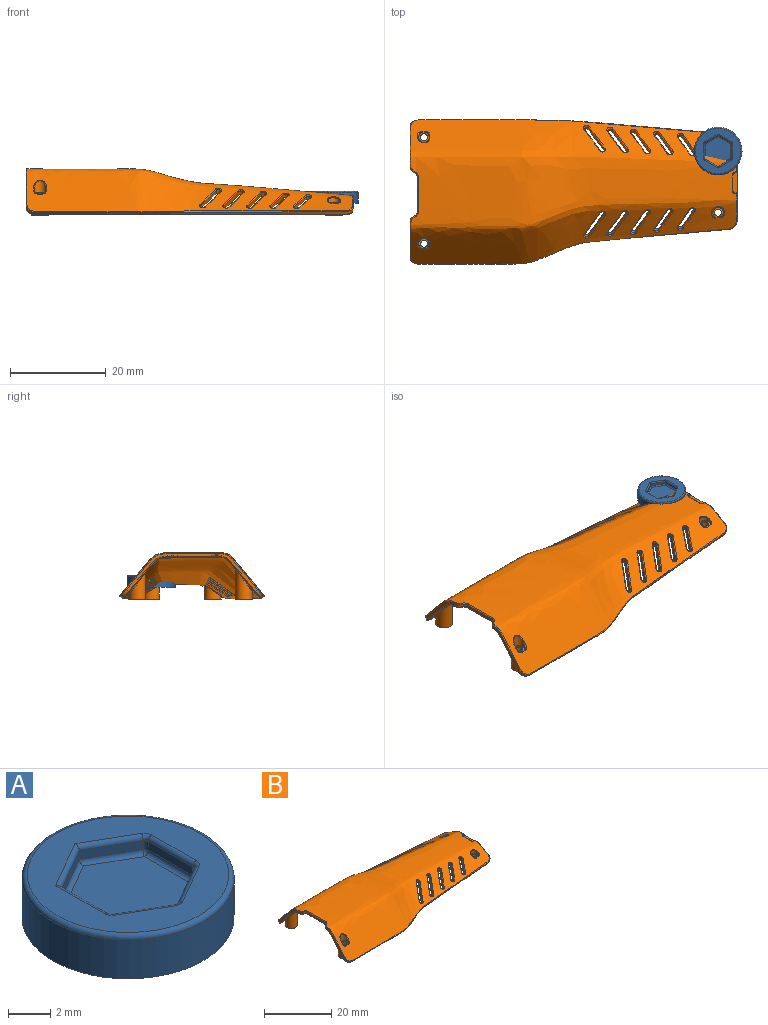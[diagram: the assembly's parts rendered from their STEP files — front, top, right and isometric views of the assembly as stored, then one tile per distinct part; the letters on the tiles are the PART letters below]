
ASSEMBLY  parts=2 mates=1
PART A: 35 faces, bbox 10.8x10.8x2.5 mm
  f0: plane 9.5x9.5mm, normal (0,0,1), area 38.4mm2, adj f16,f20,f21,f25,f26,f28,f29,f31
  f1: cylinder r=5mm len=10mm, axis (0,0,-1), area 70.7mm2, adj f2,f34
  f2: plane 10x10mm, normal (0,0,-1), area 78.5mm2, adj f1
  f3: plane 2.56x1.48mm, normal (0.5,0.87,0), area 1.5mm2, adj f11,f12,f19,f20
  f4: plane 2.56x1.48mm, normal (-0.5,0.87,0), area 1.5mm2, adj f12,f13,f21,f22
  f5: plane 2.96x0.5mm, normal (-1,0,0), area 1.5mm2, adj f22,f23,f29,f30
  f6: plane 2.69x1.55mm, normal (-0.5,-0.87,0), area 1.6mm2, adj f7,f24,f30,f33
  f7: plane 2.81x1.63mm, normal (0.5,-0.87,0), area 1.6mm2, adj f6,f8,f18,f31
  f8: plane 3.11x0.5mm, normal (1,0,0), area 1.6mm2, adj f7,f14,f19,f28
  f9: plane 5.92x5.13mm, normal (0,0,1), area 22.8mm2, adj f11,f13,f14,f18,f23,f24
  f10: sphere r=0.25mm, area 0.1mm2, adj f11,f12,f13
  f11: cylinder r=0.25mm len=2.69mm, axis (0.87,-0.5,0), area 1.2mm2, adj f3,f9,f10,f15
  f12: cylinder r=0.25mm len=0.5mm, axis (0,0,-1), area 0.1mm2, adj f3,f4,f10,f16
  f13: cylinder r=0.25mm len=2.69mm, axis (0.87,0.5,0), area 1.2mm2, adj f4,f9,f10,f17
  f14: cylinder r=0.25mm len=3.11mm, axis (0,-1,0), area 1.2mm2, adj f8,f9,f15,f18
  f15: sphere r=0.25mm, area 0.1mm2, adj f11,f14,f19
  f16: torus R=0.5mm, axis (0,0,1), area 0.1mm2, adj f0,f12,f20,f21
  f17: sphere r=0.25mm, area 0.1mm2, adj f13,f22,f23
  f18: cylinder r=0.25mm len=2.94mm, axis (-0.87,-0.5,0), area 1.2mm2, adj f7,f9,f14,f24
  f19: cylinder r=0.25mm len=0.5mm, axis (0,0,-1), area 0.1mm2, adj f3,f8,f15,f25
  f20: cylinder r=0.25mm len=2.69mm, axis (-0.87,0.5,0), area 1.2mm2, adj f0,f3,f16,f25
  f21: cylinder r=0.25mm len=2.69mm, axis (-0.87,-0.5,0), area 1.2mm2, adj f0,f4,f16,f26
  f22: cylinder r=0.25mm len=0.5mm, axis (0,0,-1), area 0.1mm2, adj f4,f5,f17,f26
  f23: cylinder r=0.25mm len=2.96mm, axis (0,1,0), area 1.2mm2, adj f5,f9,f17,f27
  f24: cylinder r=0.25mm len=2.81mm, axis (-0.87,0.5,0), area 1.2mm2, adj f6,f9,f18,f27
  f25: torus R=0.5mm, axis (0,0,1), area 0.1mm2, adj f0,f19,f20,f28
  f26: torus R=0.5mm, axis (0,0,1), area 0.1mm2, adj f0,f21,f22,f29
  f27: sphere r=0.25mm, area 0.1mm2, adj f23,f24,f30
  f28: cylinder r=0.25mm len=3.25mm, axis (0,1,0), area 1.2mm2, adj f0,f8,f25,f31
  f29: cylinder r=0.25mm len=2.96mm, axis (0,-1,0), area 1.2mm2, adj f0,f5,f26,f32
  f30: cylinder r=0.25mm len=0.5mm, axis (0,0,-1), area 0.1mm2, adj f5,f6,f27,f32
  f31: cylinder r=0.25mm len=3.19mm, axis (0.87,0.5,0), area 1.3mm2, adj f0,f7,f28,f33
  f32: torus R=0.5mm, axis (0,0,1), area 0.1mm2, adj f0,f29,f30,f33
  f33: cylinder r=0.25mm len=2.94mm, axis (0.87,-0.5,0), area 1.2mm2, adj f0,f6,f31,f32
  f34: torus R=4.75mm, axis (0,0,1), area 12.1mm2, adj f0,f1
PART B: 192 faces, bbox 76.3x36.1x14.9 mm
  f0: offset ~73.33x31.03mm, area 1976.2mm2, adj f1,f114,f115,f116,f117,f118,f119,f120
  f1: bspline ~2.79x2.08mm, area 1.4mm2, adj f0,f2,f114,f116
  f2: cylinder r=1.2mm len=2.39mm, axis (0,0,1), area 0mm2, adj f1,f3
  f3: torus R=1.1mm, axis (0,0,1), area 0.8mm2, adj f2,f4,f114,f116
  f4: plane 2.19x2.1mm, normal (0,0,1), area 2mm2, adj f3,f5,f115
  f5: cylinder r=0.72mm len=2.5mm, axis (0,0,-1), area 11.4mm2, adj f4,f6
  f6: plane 3.46x3.46mm, normal (0,0,-1), area 7.8mm2, adj f5,f7
  f7: cylinder r=1.73mm len=3.46mm, axis (0,0,-1), area 18.4mm2, adj f6,f8
  f8: bspline ~3.87x3.87mm, area 3.9mm2, adj f7,f9
  f9: bspline ~71.92x28.74mm, area 1873.9mm2, adj f8,f10,f11,f12,f13,f14,f15,f16
  f10: plane 4.4x3.43mm, normal (0.86,-0.42,-0.3), area 4.6mm2, adj f9,f11,f13,f168
  f11: cylinder r=0.5mm len=1.16mm, axis (0.06,-0.49,0.87), area 1.3mm2, adj f9,f10,f12,f169
  f12: plane 4.39x3.4mm, normal (-0.86,0.42,0.3), area 4.4mm2, adj f9,f11,f13,f170
  f13: cylinder r=0.5mm len=1.17mm, axis (0.06,-0.49,0.87), area 1.3mm2, adj f9,f10,f12,f171
  f14: plane 3.96x2.85mm, normal (0.86,-0.42,-0.3), area 3.9mm2, adj f9,f15,f17,f160
  f15: cylinder r=0.5mm len=1.13mm, axis (0.06,-0.49,0.87), area 1.3mm2, adj f9,f14,f16,f161
  f16: plane 4.51x3.37mm, normal (-0.86,0.42,0.3), area 3.8mm2, adj f9,f15,f17,f162
  f17: cylinder r=0.5mm len=1.14mm, axis (0.06,-0.49,0.87), area 1.3mm2, adj f9,f14,f16,f163
  f18: plane 4.91x3.9mm, normal (0.86,-0.42,-0.3), area 5.3mm2, adj f9,f19,f21,f152
  f19: cylinder r=0.5mm len=1.23mm, axis (0.06,-0.49,0.87), area 1.3mm2, adj f9,f18,f20,f153
  f20: plane 4.87x3.9mm, normal (-0.86,0.42,0.3), area 5mm2, adj f9,f19,f21,f154
  f21: cylinder r=0.5mm len=1.19mm, axis (0.06,-0.49,0.87), area 1.3mm2, adj f9,f18,f20,f155
  f22: bspline ~3.88x3.87mm, area 3.9mm2, adj f9,f23
  f23: cylinder r=1.73mm len=3.46mm, axis (0,0,-1), area 18.8mm2, adj f22,f24
  f24: plane 3.46x3.46mm, normal (0,0,-1), area 7.8mm2, adj f23,f25
  f25: cylinder r=0.72mm len=2.5mm, axis (0,0,-1), area 11.4mm2, adj f24,f26
  f26: plane 2.19x2.14mm, normal (0,0,1), area 2.1mm2, adj f25,f27,f119
  f27: torus R=1.1mm, axis (0,0,1), area 0.8mm2, adj f26,f28,f118,f120
  f28: cylinder r=1.2mm len=2.39mm, axis (0,0,1), area 0mm2, adj f27,f117
  f29: bspline ~4.77x3.87mm, area 4.7mm2, adj f9,f30
  f30: cylinder r=1.73mm len=5.55mm, axis (0,0,-1), area 35.1mm2, adj f29,f31
  f31: plane 3.46x3.46mm, normal (0,0,-1), area 7.8mm2, adj f30,f32
  f32: cylinder r=0.72mm len=3.82mm, axis (0,0,-1), area 17.3mm2, adj f31,f33
  f33: plane 2.19x2.07mm, normal (0,0,1), area 2.1mm2, adj f32,f34,f127
  f34: torus R=1.1mm, axis (0,0,1), area 0.9mm2, adj f33,f35,f126,f128
  f35: cylinder r=1.2mm len=2.55mm, axis (0,0,1), area 7.8mm2, adj f34,f125
  f36: bspline ~4.77x3.87mm, area 4.7mm2, adj f9,f37
  f37: cylinder r=1.73mm len=6.29mm, axis (0,0,-1), area 43.1mm2, adj f36,f38
  f38: plane 3.46x3.46mm, normal (0,0,-1), area 7.8mm2, adj f37,f39
  f39: cylinder r=0.72mm len=4.5mm, axis (0,0,-1), area 20.4mm2, adj f38,f40
  f40: plane 2.19x2.12mm, normal (0,0,1), area 2.1mm2, adj f39,f41,f122
  f41: torus R=1.1mm, axis (0,0,1), area 0.9mm2, adj f40,f42,f121,f123
  f42: cylinder r=1.2mm len=2.61mm, axis (0,0,1), area 8.1mm2, adj f41,f124
  f43: plane 4.18x3.14mm, normal (0.86,-0.42,-0.3), area 4.3mm2, adj f9,f44,f46,f156
  f44: cylinder r=0.5mm len=1.15mm, axis (0.06,-0.49,0.87), area 1.3mm2, adj f9,f43,f45,f157
  f45: plane 4.78x3.71mm, normal (-0.86,0.42,0.3), area 4.1mm2, adj f9,f44,f46,f158
  f46: cylinder r=0.5mm len=1.16mm, axis (0.06,-0.49,0.87), area 1.3mm2, adj f9,f43,f45,f159
  f47: plane 4.62x3.72mm, normal (0.86,-0.42,-0.3), area 4.9mm2, adj f9,f48,f50,f164
  f48: cylinder r=0.5mm len=1.17mm, axis (0.06,-0.49,0.87), area 1.3mm2, adj f9,f47,f49,f165
  f49: plane 4.61x3.68mm, normal (-0.86,0.42,0.3), area 4.7mm2, adj f9,f48,f50,f166
  f50: cylinder r=0.5mm len=1.18mm, axis (0.06,-0.49,0.87), area 1.3mm2, adj f9,f47,f49,f167
  f51: cylinder r=0.5mm len=1.18mm, axis (0.06,0.49,0.87), area 1.3mm2, adj f9,f52,f54,f175
  f52: plane 4.85x3.98mm, normal (0.86,0.42,-0.3), area 5.3mm2, adj f9,f51,f53,f172
  f53: cylinder r=0.5mm len=1.18mm, axis (0.06,0.49,0.87), area 1.3mm2, adj f9,f52,f54,f173
  f54: plane 4.84x3.95mm, normal (-0.86,-0.42,0.3), area 5.1mm2, adj f9,f51,f53,f174
  f55: cylinder r=0.5mm len=1.15mm, axis (0.06,0.49,0.87), area 1.3mm2, adj f9,f56,f58,f179
  f56: plane 4.18x3.14mm, normal (0.86,0.42,-0.3), area 4.3mm2, adj f9,f55,f57,f176
  f57: cylinder r=0.5mm len=1.16mm, axis (0.06,0.49,0.87), area 1.3mm2, adj f9,f56,f58,f177
  f58: plane 4.18x3.11mm, normal (-0.86,-0.42,0.3), area 4.1mm2, adj f9,f55,f57,f178
  f59: cylinder r=0.5mm len=1.13mm, axis (0.06,0.49,0.87), area 1.3mm2, adj f9,f60,f62,f183
  f60: plane 3.96x2.85mm, normal (0.86,0.42,-0.3), area 3.9mm2, adj f9,f59,f61,f180
  f61: cylinder r=0.5mm len=1.14mm, axis (0.06,0.49,0.87), area 1.3mm2, adj f9,f60,f62,f181
  f62: plane 4.56x3.42mm, normal (-0.86,-0.42,0.3), area 3.8mm2, adj f9,f59,f61,f182
  f63: cylinder r=0.5mm len=1.17mm, axis (0.06,0.49,0.87), area 1.3mm2, adj f9,f64,f66,f187
  f64: plane 4.62x3.71mm, normal (0.86,0.42,-0.3), area 4.9mm2, adj f9,f63,f65,f184
  f65: cylinder r=0.5mm len=1.18mm, axis (0.06,0.49,0.87), area 1.3mm2, adj f9,f64,f66,f185
  f66: plane 4.61x3.68mm, normal (-0.86,-0.42,0.3), area 4.7mm2, adj f9,f63,f65,f186
  f67: cylinder r=0.5mm len=1.16mm, axis (0.06,0.49,0.87), area 1.3mm2, adj f9,f68,f70,f191
  f68: plane 4.4x3.43mm, normal (0.86,0.42,-0.3), area 4.6mm2, adj f9,f67,f69,f188
  f69: cylinder r=0.5mm len=1.17mm, axis (0.06,0.49,0.87), area 1.3mm2, adj f9,f68,f70,f189
  f70: plane 4.39x3.39mm, normal (-0.86,-0.42,0.3), area 4.4mm2, adj f9,f67,f69,f190
  f71: bspline ~2.84x1.86mm, area 0.2mm2, adj f9,f72,f99,f113
  f72: plane 0.6x0.55mm, normal (-0.53,-0.85,0), area 0.4mm2, adj f71,f73,f98,f143
  f73: cylinder r=1.04mm len=0.88mm, axis (0,0,-1), area 0.6mm2, adj f72,f74,f113,f142
  f74: plane 7.18x0.6mm, normal (-1,0,0), area 4.3mm2, adj f73,f75,f112,f141
  f75: cylinder r=1.04mm len=0.88mm, axis (0,0,-1), area 0.6mm2, adj f74,f76,f111,f140
  f76: plane 0.6x0.55mm, normal (-0.53,0.85,0), area 0.4mm2, adj f75,f77,f110,f139
  f77: bspline ~1.16x0.88mm, area 0.6mm2, adj f76,f78,f109,f138
  f78: bspline ~9.69x9.57mm, area 6.3mm2, adj f77,f79,f108,f137
  f79: bspline ~2.15x2.01mm, area 1.9mm2, adj f78,f80,f107,f136
  f80: bspline ~68.31x7.89mm, area 39.2mm2, adj f79,f81,f106,f135
  f81: bspline ~2.17x1.89mm, area 1.8mm2, adj f80,f82,f105,f134
  f82: bspline ~19.72x4.02mm, area 9.9mm2, adj f81,f83,f87,f94,f95,f104,f133,f149
  f83: bspline ~2.16x1.89mm, area 1.8mm2, adj f82,f84,f103,f148
  f84: bspline ~68.31x3.62mm, area 38.7mm2, adj f83,f85,f102,f147
  f85: bspline ~2.15x2.01mm, area 1.9mm2, adj f84,f86,f101,f146
  f86: bspline ~10.2x9.69mm, area 6.9mm2, adj f85,f98,f100,f145
  f87: bspline ~0.31x0.13mm, area 0mm2, adj f82,f88,f93,f94
  f88: plane 0.39x0.13mm, normal (0,-1,0), area 0mm2, adj f87,f89,f94,f150
  f89: cylinder r=0.41mm len=0.41mm, axis (0,0,1), area 0.1mm2, adj f88,f90,f94,f129
  f90: plane 3.31x0.19mm, normal (1,0,0), area 0.6mm2, adj f89,f91,f94,f130
  f91: cylinder r=0.41mm len=0.41mm, axis (0,0,1), area 0.1mm2, adj f90,f92,f94,f131
  f92: plane 0.39x0.13mm, normal (0,1,0), area 0mm2, adj f91,f94,f95,f132
  f93: bspline ~0.27x0.2mm, area 0mm2, adj f87,f149,f150
  f94: plane 4.33x0.9mm, normal (0,0,1), area 3.6mm2, adj f82,f87,f88,f89,f90,f91,f92,f95
  f95: bspline ~0.31x0.13mm, area 0mm2, adj f82,f92,f94,f96
  f96: bspline ~0.1x0.1mm, area 0mm2, adj f95,f97,f132
  f97: bspline ~0.27x0.2mm, area 0mm2, adj f96,f132,f133
  f98: bspline ~0.94x0.88mm, area 0.6mm2, adj f72,f86,f99,f144
  f99: bspline ~1.15x0.64mm, area 0.3mm2, adj f9,f71,f98,f100
  f100: bspline ~9.59x8.38mm, area 3.5mm2, adj f9,f86,f99,f101
  f101: bspline ~2.45x1.75mm, area 1mm2, adj f9,f85,f100,f102
  f102: bspline ~66.24x3.14mm, area 20.3mm2, adj f9,f84,f101,f103
  f103: bspline ~2.31x2.29mm, area 0.9mm2, adj f9,f83,f102,f104
  f104: bspline ~18.07x2.98mm, area 5.2mm2, adj f9,f82,f103,f105
  f105: bspline ~2.31x1.99mm, area 0.9mm2, adj f9,f81,f104,f106
  f106: bspline ~66.11x7.41mm, area 20.5mm2, adj f9,f80,f105,f107
  f107: bspline ~2.45x2.01mm, area 1mm2, adj f9,f79,f106,f108
  f108: bspline ~8.57x8.38mm, area 3.2mm2, adj f9,f78,f107,f109
  f109: bspline ~1.04x0.77mm, area 0.3mm2, adj f9,f77,f108,f110
  f110: bspline ~2.29x1.52mm, area 0.2mm2, adj f9,f76,f109,f111
  f111: bspline ~1.45x0.9mm, area 0.4mm2, adj f9,f75,f110,f112
  f112: bspline ~8.19x0.2mm, area 2.3mm2, adj f9,f74,f111,f113
  f113: bspline ~1.37x0.74mm, area 0.4mm2, adj f9,f71,f73,f112
  f114: bspline ~0.87x0.69mm, area 0.2mm2, adj f0,f1,f3,f115
  f115: bspline ~4.03x0.63mm, area 0.1mm2, adj f0,f4,f114,f116
  f116: bspline ~0.87x0.72mm, area 0.2mm2, adj f0,f1,f3,f115
  f117: bspline ~2.8x2.34mm, area 1.5mm2, adj f0,f28,f118,f120
  f118: bspline ~0.89x0.82mm, area 0.2mm2, adj f0,f27,f117,f119
  f119: bspline ~4.6x0.72mm, area 0.1mm2, adj f0,f26,f118,f120
  f120: bspline ~1.02x0.61mm, area 0.2mm2, adj f0,f27,f117,f119
  f121: bspline ~0.92x0.56mm, area 0.2mm2, adj f0,f41,f122,f124
  f122: bspline ~3.99x0.15mm, area 0.1mm2, adj f0,f40,f121,f123
  f123: bspline ~0.99x0.56mm, area 0.2mm2, adj f0,f41,f122,f124
  f124: bspline ~3.05x2.8mm, area 2mm2, adj f0,f42,f121,f123
  f125: bspline ~3x2.8mm, area 2mm2, adj f0,f35,f126,f128
  f126: bspline ~0.75x0.55mm, area 0.2mm2, adj f0,f34,f125,f127
  f127: bspline ~5.1x0.15mm, area 0.2mm2, adj f0,f33,f126,f128
  f128: bspline ~0.86x0.52mm, area 0.2mm2, adj f0,f34,f125,f127
  f129: bspline ~0.74x0.64mm, area 0.2mm2, adj f0,f89,f130,f150
  f130: bspline ~4.12x0.2mm, area 1mm2, adj f0,f90,f129,f131
  f131: bspline ~0.74x0.64mm, area 0.2mm2, adj f0,f91,f130,f132
  f132: bspline ~11.04x1.21mm, area 0.1mm2, adj f0,f92,f96,f97,f131
  f133: bspline ~11.24x5.04mm, area 2mm2, adj f0,f82,f97,f134
  f134: bspline ~2.3x2.27mm, area 0.9mm2, adj f0,f81,f133,f135
  f135: bspline ~68.53x7.55mm, area 20.5mm2, adj f0,f80,f134,f136
  f136: bspline ~2.45x2.01mm, area 1mm2, adj f0,f79,f135,f137
  f137: bspline ~9.18x8.67mm, area 3.4mm2, adj f0,f78,f136,f138
  f138: bspline ~1.06x0.77mm, area 0.3mm2, adj f0,f77,f137,f139
  f139: bspline ~2.85x1.88mm, area 0.2mm2, adj f0,f76,f138,f140
  f140: bspline ~1.25x0.9mm, area 0.4mm2, adj f0,f75,f139,f141
  f141: bspline ~8.67x0.2mm, area 2.3mm2, adj f0,f74,f140,f142
  f142: bspline ~1.37x0.74mm, area 0.4mm2, adj f0,f73,f141,f143
  f143: bspline ~2.84x1.87mm, area 0.2mm2, adj f0,f72,f142,f144
  f144: bspline ~1.15x0.64mm, area 0.3mm2, adj f0,f98,f143,f145
  f145: bspline ~10.2x8.67mm, area 3.7mm2, adj f0,f86,f144,f146
  f146: bspline ~2.45x2.01mm, area 1mm2, adj f0,f85,f145,f147
  f147: bspline ~66.49x3.3mm, area 20.3mm2, adj f0,f84,f146,f148
  f148: bspline ~2.3x1.98mm, area 0.9mm2, adj f0,f83,f147,f149
  f149: bspline ~11.73x5.04mm, area 2.1mm2, adj f0,f82,f93,f148
  f150: bspline ~11.24x1.23mm, area 0.1mm2, adj f0,f88,f93,f129,f151
  f151: bspline ~0.11x0.11mm, area 0mm2, adj f150
  f152: bspline ~5.58x4.15mm, area 1.9mm2, adj f0,f18,f153,f155
  f153: bspline ~1.35x0.86mm, area 0.6mm2, adj f0,f19,f152,f154
  f154: bspline ~7.51x5.55mm, area 2.1mm2, adj f0,f20,f153,f155
  f155: bspline ~1.36x0.85mm, area 0.5mm2, adj f0,f21,f152,f154
  f156: bspline ~8.01x5.84mm, area 1.6mm2, adj f0,f43,f157,f159
  f157: bspline ~1.36x0.9mm, area 0.6mm2, adj f0,f44,f156,f158
  f158: bspline ~8.29x5.97mm, area 1.7mm2, adj f0,f45,f157,f159
  f159: bspline ~1.36x0.88mm, area 0.6mm2, adj f0,f46,f156,f158
  f160: bspline ~11.03x7.92mm, area 1.5mm2, adj f0,f14,f161,f163
  f161: bspline ~1.37x0.91mm, area 0.6mm2, adj f0,f15,f160,f162
  f162: bspline ~11.31x8.05mm, area 1.6mm2, adj f0,f16,f161,f163
  f163: bspline ~1.36x0.9mm, area 0.6mm2, adj f0,f17,f160,f162
  f164: bspline ~6.52x4.88mm, area 1.8mm2, adj f0,f47,f165,f167
  f165: bspline ~1.36x0.89mm, area 0.6mm2, adj f0,f48,f164,f166
  f166: bspline ~7.12x5.26mm, area 2mm2, adj f0,f49,f165,f167
  f167: bspline ~1.36x0.86mm, area 0.5mm2, adj f0,f50,f164,f166
  f168: bspline ~8.46x6.25mm, area 1.7mm2, adj f0,f10,f169,f171
  f169: bspline ~1.36x0.89mm, area 0.6mm2, adj f0,f11,f168,f170
  f170: bspline ~5.55x4.05mm, area 1.8mm2, adj f0,f12,f169,f171
  f171: bspline ~1.36x0.87mm, area 0.6mm2, adj f0,f13,f168,f170
  f172: bspline ~6.97x5.32mm, area 1.9mm2, adj f0,f52,f173,f175
  f173: bspline ~1.32x0.94mm, area 0.6mm2, adj f0,f53,f172,f174
  f174: bspline ~7.49x5.6mm, area 2.1mm2, adj f0,f54,f173,f175
  f175: bspline ~1.32x0.93mm, area 0.6mm2, adj f0,f51,f172,f174
  f176: bspline ~7.88x5.74mm, area 1.6mm2, adj f0,f56,f177,f179
  f177: bspline ~1.32x0.97mm, area 0.6mm2, adj f0,f57,f176,f178
  f178: bspline ~6.17x4.43mm, area 1.7mm2, adj f0,f58,f177,f179
  f179: bspline ~1.32x0.95mm, area 0.6mm2, adj f0,f55,f176,f178
  f180: bspline ~10.93x7.85mm, area 1.5mm2, adj f0,f60,f181,f183
  f181: bspline ~1.32x0.99mm, area 0.6mm2, adj f0,f61,f180,f182
  f182: bspline ~11.08x7.89mm, area 1.6mm2, adj f0,f62,f181,f183
  f183: bspline ~1.32x0.97mm, area 0.6mm2, adj f0,f59,f180,f182
  f184: bspline ~6.6x4.94mm, area 1.8mm2, adj f0,f64,f185,f187
  f185: bspline ~1.32x0.95mm, area 0.6mm2, adj f0,f65,f184,f186
  f186: bspline ~7.14x5.28mm, area 2mm2, adj f0,f66,f185,f187
  f187: bspline ~1.32x0.94mm, area 0.6mm2, adj f0,f63,f184,f186
  f188: bspline ~8.22x6.08mm, area 1.7mm2, adj f0,f68,f189,f191
  f189: bspline ~1.32x0.96mm, area 0.6mm2, adj f0,f69,f188,f190
  f190: bspline ~6.43x4.69mm, area 1.8mm2, adj f0,f70,f189,f191
  f191: bspline ~1.32x0.94mm, area 0.6mm2, adj f0,f67,f188,f190
PLACE A t=(30.19,6.41,1.9)mm
PLACE B at identity fixed
MATE fastened A.f1 <-> B.f23  axis (0,0,-1) through (30.19,6.41,1.9)mm
